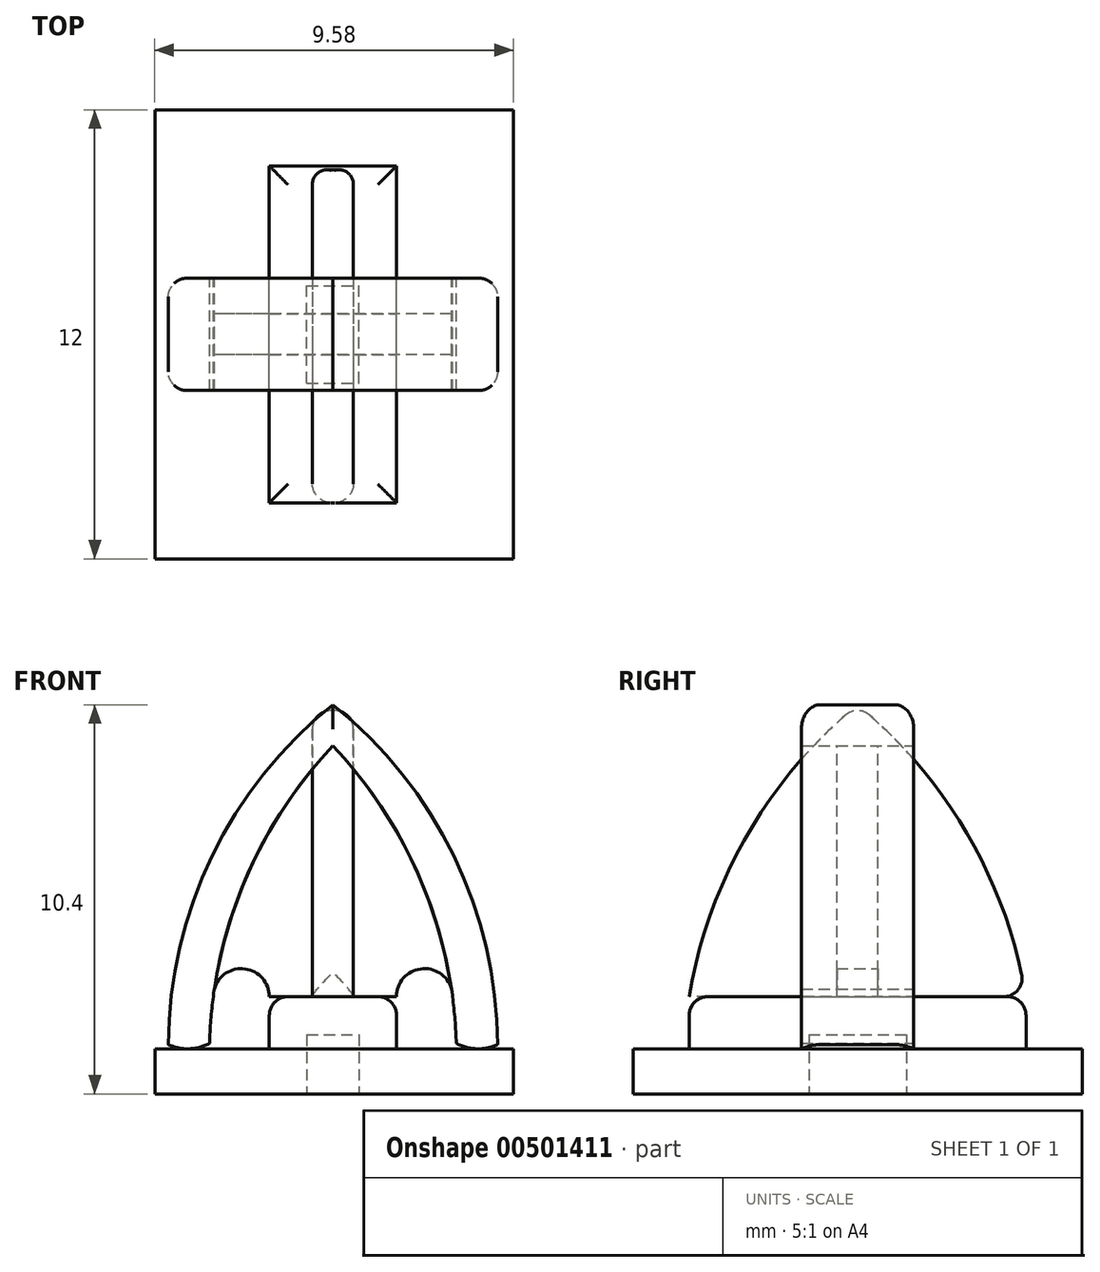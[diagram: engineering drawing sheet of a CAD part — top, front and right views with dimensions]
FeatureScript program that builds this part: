
annotation { "Feature Type Name" : "Feature", "Feature Type Description" : "" }
export const myFeature = defineFeature(function(context is Context, id is Id, definition is map)
    precondition{}
    {
        {
            var Q0;
            Q0=qCreatedBy(makeId("Front.planeOp"),FACE);
            var sketch = newSketch(context, id + "F0", { "sketchPlane" : qUnion([Q0])});
            skLineSegment(sketch, "E0", {"start": v(-20.55, 0) * mm, "end": v(18.75, 0) * mm, "construction": true});
            skLineSegment(sketch, "E1", {"start": v(0, 29.45) * mm, "end": v(0, -17.38) * mm, "construction": true});
            skLineSegment(sketch, "E2.bottom", {"start": v(-1.7, 1.4) * mm, "end": v(1.7, 1.4) * mm});
            skLineSegment(sketch, "E2.top", {"start": v(-1.7, 0) * mm, "end": v(1.7, 0) * mm});
            skLineSegment(sketch, "E2.left", {"start": v(-1.7, 1.4) * mm, "end": v(-1.7, 0) * mm});
            skLineSegment(sketch, "E2.right", {"start": v(1.7, 1.4) * mm, "end": v(1.7, 0) * mm});
            skLineSegment(sketch, "E3", {"start": v(-2, 9.2) * mm, "end": v(5.18, 9.2) * mm, "construction": true});
            skLineSegment(sketch, "E4", {"start": v(-4.4, 8.99) * mm, "end": v(-4.4, 1.4) * mm, "construction": true});
            skLineSegment(sketch, "E5", {"start": v(4.4, 10.44) * mm, "end": v(4.4, -2.92) * mm, "construction": true});
            skArc(sketch, "E6", {"start": v(0, 9.2) * mm, "mid": v(-3.23, 5.16) * mm, "end": v(-4.4, 0.12) * mm});
            skArc(sketch, "E7.MirrorCS", {"start": v(0, 9.2) * mm, "mid": v(3.26, 5.1) * mm, "end": v(4.4, 0) * mm});
            skArc(sketch, "E8", {"start": v(0, 8.1) * mm, "mid": v(-2.38, 4.43) * mm, "end": v(-3.3, 0.15) * mm});
            skLineSegment(sketch, "E9", {"start": v(-1.7, 1.4) * mm, "end": v(-5.86, 1.4) * mm, "construction": true});
            skArc(sketch, "E10", {"start": v(-1.7, 1.4) * mm, "mid": v(-2.45, 2.15) * mm, "end": v(-3.2, 1.4) * mm});
            skArc(sketch, "E11.MirrorCS", {"start": v(0, 8.1) * mm, "mid": v(2.41, 4.36) * mm, "end": v(3.3, 0) * mm});
            skArc(sketch, "E12.MirrorCS", {"start": v(1.7, 1.4) * mm, "mid": v(2.45, 2.15) * mm, "end": v(3.2, 1.4) * mm});
            skArc(sketch, "E13", {"start": v(-4.4, 0.12) * mm, "mid": v(-3.84, 0) * mm, "end": v(-3.3, 0.15) * mm});
            skLineSegment(sketch, "E14.trimOffspring", {"start": v(-4.4, 0) * mm, "end": v(-4.4, -2.36) * mm, "construction": true});
            skPoint(sketch, "E15.orphan", {"position": v(-3.3, 0) * mm});
            skArc(sketch, "E16.MirrorCS", {"start": v(4.4, 0.12) * mm, "mid": v(3.84, 0) * mm, "end": v(3.3, 0.15) * mm});
            skLineSegment(sketch, "E17.bottom", {"start": v(-4.76, 0) * mm, "end": v(4.82, 0) * mm});
            skLineSegment(sketch, "E17.top", {"start": v(-4.76, -1.2) * mm, "end": v(4.82, -1.2) * mm});
            skLineSegment(sketch, "E17.left", {"start": v(-4.76, 0) * mm, "end": v(-4.76, -1.2) * mm});
            skLineSegment(sketch, "E17.right", {"start": v(4.82, 0) * mm, "end": v(4.82, -1.2) * mm});
            skSolve(sketch);
        }
        {
            var Q0;
            Q0=makeQuery(id+"F0.imprint","IMPRINT",FACE,{"disambiguationData":[TD([[makeQuery(id+"F0.imprint","IMPRINT",EDGE,{"derivedFrom":sQuery(id+"F0.wireOp",EDGE,"E2.bottom")}),-1.0]])]});
            extrude(context, id + "F1", {"entities" : qUnion([Q0]), "endBound" : BoundingType.SYMMETRIC, "depth" : 9 * mm, "offsetDistance" : 25 * mm});
        }
        {
            var Q0;
            {var subQ9=sQuery(id+"F0.wireOp",EDGE,"E6");Q0=makeQuery(id+"F0.imprint","IMPRINT",FACE,{"disambiguationData":[TD([[makeQuery(id+"F0.imprint","IMPRINT",EDGE,{"derivedFrom":subQ9}),1.0]])]});}
            extrude(context, id + "F2", {"entities" : qUnion([Q0]), "endBound" : BoundingType.SYMMETRIC, "depth" : 3 * mm, "offsetDistance" : 25 * mm});
        }
        {
            var Q0;
            {var subQ1=sQuery(id+"F0.wireOp",EDGE,"E2.bottom");Q0=makeQuery(id+"F0.imprint","IMPRINT",FACE,{"disambiguationData":[TD([[makeQuery(id+"F0.imprint","IMPRINT",EDGE,{"derivedFrom":subQ1}),1.0]])]});}
            extrude(context, id + "F3", {"entities" : qUnion([Q0]), "endBound" : BoundingType.SYMMETRIC, "depth" : 1.1 * mm, "offsetDistance" : 25 * mm});
        }
        {
            var Q0;
            Q0=makeQuery(id+"F0.imprint","IMPRINT",FACE,{"disambiguationData":[TD([[makeQuery(id+"F0.imprint","IMPRINT",EDGE,{"derivedFrom":sQuery(id+"F0.wireOp",EDGE,"E17.top")}),1.0]])]});
            extrude(context, id + "F4", {"entities" : qUnion([Q0]), "operationType" : NewBodyOperationType.ADD, "endBound" : BoundingType.SYMMETRIC, "depth" : 12 * mm, "offsetDistance" : 25 * mm});
        }
        {
            var Q0;
            Q0=qCreatedBy(makeId("Right.planeOp"),FACE);
            var sketch = newSketch(context, id + "F5", { "sketchPlane" : qUnion([Q0])});
            skLineSegment(sketch, "E18", {"start": v(0, 9.2) * mm, "end": v(-3.38, 9.2) * mm, "construction": true});
            skArc(sketch, "E19", {"start": v(4.5, 1.4) * mm, "mid": v(2.96, 5.7) * mm, "end": v(0, 9.2) * mm});
            skLineSegment(sketch, "E20", {"start": v(0, 18.1) * mm, "end": v(0, -4.27) * mm, "construction": true});
            skArc(sketch, "E21.MirrorCS", {"start": v(-4.5, 1.4) * mm, "mid": v(-2.96, 5.7) * mm, "end": v(0, 9.2) * mm});
            skLineSegment(sketch, "E22", {"start": v(4.5, 1.4) * mm, "end": v(-4.5, 1.4) * mm});
            skSolve(sketch);
        }
        {
            var Q0;
            Q0 = qSketchRegion(id + "F5", true);
            extrude(context, id + "F6", {"entities" : qUnion([Q0]), "endBound" : BoundingType.SYMMETRIC, "depth" : 1.1 * mm, "offsetDistance" : 25 * mm});
        }
        {
            var Q0;
            Q0=makeQuery(id+"F2.opExtrude","CAP_EDGE",EDGE,{"disambiguationData":[OSD([sQuery(id+"F0.wireOp",EDGE,"E6")])],"isStart":true});
            var Q1;
            Q1=makeQuery(id+"F2.opExtrude","CAP_EDGE",EDGE,{"disambiguationData":[OSD([sQuery(id+"F0.wireOp",EDGE,"E7.MirrorCS")])],"isStart":true});
            var Q2;
            Q2=makeQuery(id+"F2.opExtrude","CAP_EDGE",EDGE,{"disambiguationData":[OSD([sQuery(id+"F0.wireOp",EDGE,"E7.MirrorCS")])],"isStart":false});
            var Q3;
            Q3=makeQuery(id+"F2.opExtrude","CAP_EDGE",EDGE,{"disambiguationData":[OSD([sQuery(id+"F0.wireOp",EDGE,"E6")])],"isStart":false});
            var Q4;
            Q4=makeQuery(id+"F6.opExtrude","CAP_EDGE",EDGE,{"disambiguationData":[OSD([sQuery(id+"F5.wireOp",EDGE,"E21.MirrorCS")])],"isStart":true});
            var Q5;
            Q5=makeQuery(id+"F6.opExtrude","CAP_EDGE",EDGE,{"disambiguationData":[OSD([sQuery(id+"F5.wireOp",EDGE,"E21.MirrorCS")])],"isStart":false});
            var Q6;
            Q6=makeQuery(id+"F6.opExtrude","CAP_EDGE",EDGE,{"disambiguationData":[OSD([sQuery(id+"F5.wireOp",EDGE,"E19")])],"isStart":true});
            var Q7;
            Q7=makeQuery(id+"F6.opExtrude","SWEPT_FACE",FACE,{"disambiguationData":[OSD([sQuery(id+"F5.wireOp",EDGE,"E19")])]});
            var Q8;
            Q8=makeQuery(id+"F1.opExtrude","CAP_EDGE",EDGE,{"disambiguationData":[OSD([sQuery(id+"F0.wireOp",EDGE,"E2.bottom")])],"isStart":true});
            var Q9;
            Q9=makeQuery(id+"F1.opExtrude","CAP_EDGE",EDGE,{"disambiguationData":[OSD([sQuery(id+"F0.wireOp",EDGE,"E2.bottom")])],"isStart":false});
            var Q10;
            Q10=makeQuery(id+"F1.opExtrude","SWEPT_EDGE",EDGE,{"disambiguationData":[OSD([sQuery(id+"F0.wireOp",EDGE,"E2.bottom"),sQuery(id+"F0.wireOp",EDGE,"E2.right"),sQuery(id+"F0.wireOp",EDGE,"E12.MirrorCS")])]});
            var Q11;
            Q11=makeQuery(id+"F1.opExtrude","SWEPT_EDGE",EDGE,{"disambiguationData":[OSD([sQuery(id+"F0.wireOp",EDGE,"E2.bottom"),sQuery(id+"F0.wireOp",EDGE,"E2.left"),sQuery(id+"F0.wireOp",EDGE,"E10")])]});
            fillet(context, id + "F7", {"entities" : qUnion([Q0, Q1, Q2, Q3, Q4, Q5, Q6, Q7, Q8, Q9, Q10, Q11]), "radius" : .5 * mm, "tangentPropagation" : true, "allowEdgeOverflow" : false});
        }
        {
            var Q0;
            Q0=makeQuery(id+"F4.opExtrude","SWEPT_FACE",FACE,{"disambiguationData":[OSD([sQuery(id+"F0.wireOp",EDGE,"E17.top")])]});
            cPlane(context, id + "F8", {"entities" : qUnion([Q0]), "cplaneType" : CPlaneType.OFFSET, "offset" : 0 * mm, "width" : 150 * mm, "height" : 150 * mm});
        }
        {
            var Q0;
            Q0=qCreatedBy(id+"F8.planeOp",FACE);
            var sketch = newSketch(context, id + "F9", { "sketchPlane" : qUnion([Q0])});
            skLineSegment(sketch, "E23", {"start": v(6.28, 0) * mm, "end": v(-8.61, 0) * mm, "construction": true});
            skLineSegment(sketch, "E24", {"start": v(0, 0) * mm, "end": v(0, -10.07) * mm, "construction": true});
            skLineSegment(sketch, "E25", {"start": v(0, 0) * mm, "end": v(0, 2.45) * mm, "construction": true});
            skLineSegment(sketch, "E26.bottom", {"start": v(-0.7, 1.3) * mm, "end": v(0.7, 1.3) * mm});
            skLineSegment(sketch, "E26.top", {"start": v(-0.7, -1.3) * mm, "end": v(0.7, -1.3) * mm});
            skLineSegment(sketch, "E26.left", {"start": v(-0.7, 1.3) * mm, "end": v(-0.7, -1.3) * mm});
            skLineSegment(sketch, "E26.right", {"start": v(0.7, 1.3) * mm, "end": v(0.7, -1.3) * mm});
            skSolve(sketch);
        }
        {
            var Q0;
            Q0 = qSketchRegion(id + "F9", true);
            extrude(context, id + "F10", {"entities" : qUnion([Q0]), "operationType" : NewBodyOperationType.REMOVE, "oppositeDirection" : true, "depth" : 1.58 * mm, "offsetDistance" : 25 * mm});
        }
    });
